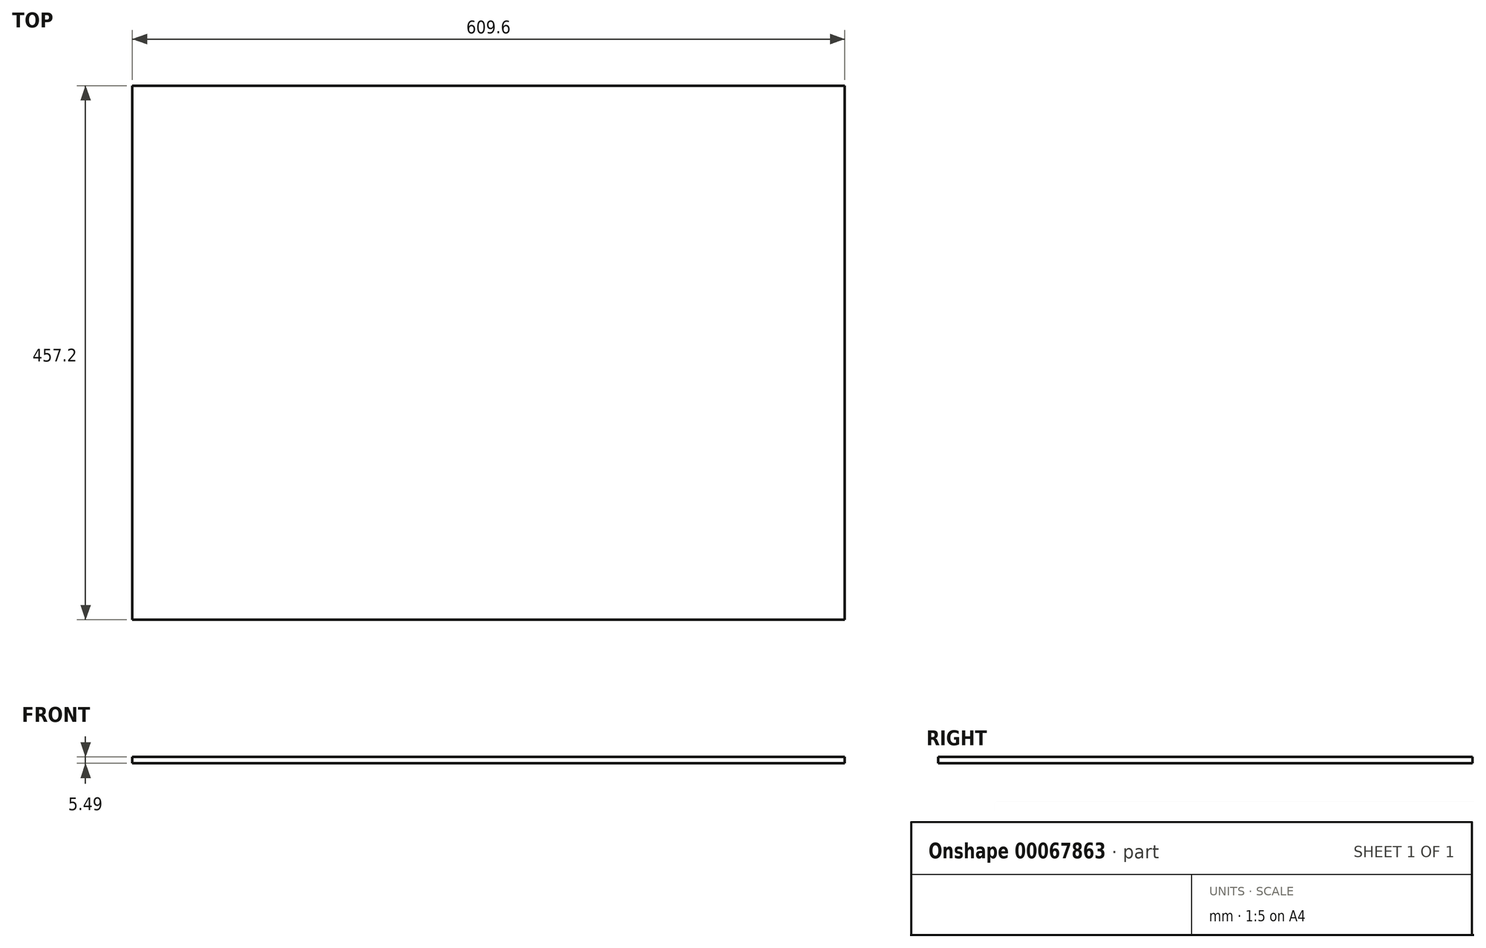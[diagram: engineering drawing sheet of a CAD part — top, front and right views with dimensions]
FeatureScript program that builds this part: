
annotation { "Feature Type Name" : "Feature", "Feature Type Description" : "" }
export const myFeature = defineFeature(function(context is Context, id is Id, definition is map)
    precondition{}
    {
        {
            var Q0;
            Q0=qCreatedBy(makeId("Top.planeOp"),FACE);
            var sketch = newSketch(context, id + "F0", { "sketchPlane" : qUnion([Q0])});
            skLineSegment(sketch, "E0.rect.bottom", {"start": v(304.8, -228.6) * mm, "end": v(0, -228.6) * mm});
            skLineSegment(sketch, "E0.rect.top", {"start": v(304.8, 228.6) * mm, "end": v(0, 228.6) * mm});
            skLineSegment(sketch, "E0.rect.left", {"start": v(304.8, -228.6) * mm, "end": v(304.8, 228.6) * mm});
            skLineSegment(sketch, "E0.rect.right", {"start": v(0, -228.6) * mm, "end": v(0, 228.6) * mm});
            skLineSegment(sketch, "E1.bottom", {"start": v(0, 228.6) * mm, "end": v(-304.8, 228.6) * mm});
            skLineSegment(sketch, "E1.top", {"start": v(0, -228.6) * mm, "end": v(-304.8, -228.6) * mm});
            skLineSegment(sketch, "E1.left", {"start": v(0, 228.6) * mm, "end": v(0, -228.6) * mm});
            skLineSegment(sketch, "E1.right", {"start": v(-304.8, 228.6) * mm, "end": v(-304.8, -228.6) * mm});
            skSolve(sketch);
        }
        {
            var Q0;
            Q0=makeQuery(id+"F0.imprint","IMPRINT",FACE,{"disambiguationData":[TD([[makeQuery(id+"F0.imprint","IMPRINT",EDGE,{"derivedFrom":sQuery(id+"F0.wireOp",EDGE,"E0.rect.bottom")}),-1.0]])]});
            var Q1;
            Q1=makeQuery(id+"F0.imprint","IMPRINT",FACE,{"disambiguationData":[TD([[makeQuery(id+"F0.imprint","IMPRINT",EDGE,{"derivedFrom":sQuery(id+"F0.wireOp",EDGE,"E1.bottom")}),1.0]])]});
            extrude(context, id + "F1", {"entities" : qUnion([Q0, Q1]), "depth" : 5.5 * mm});
        }
    });
